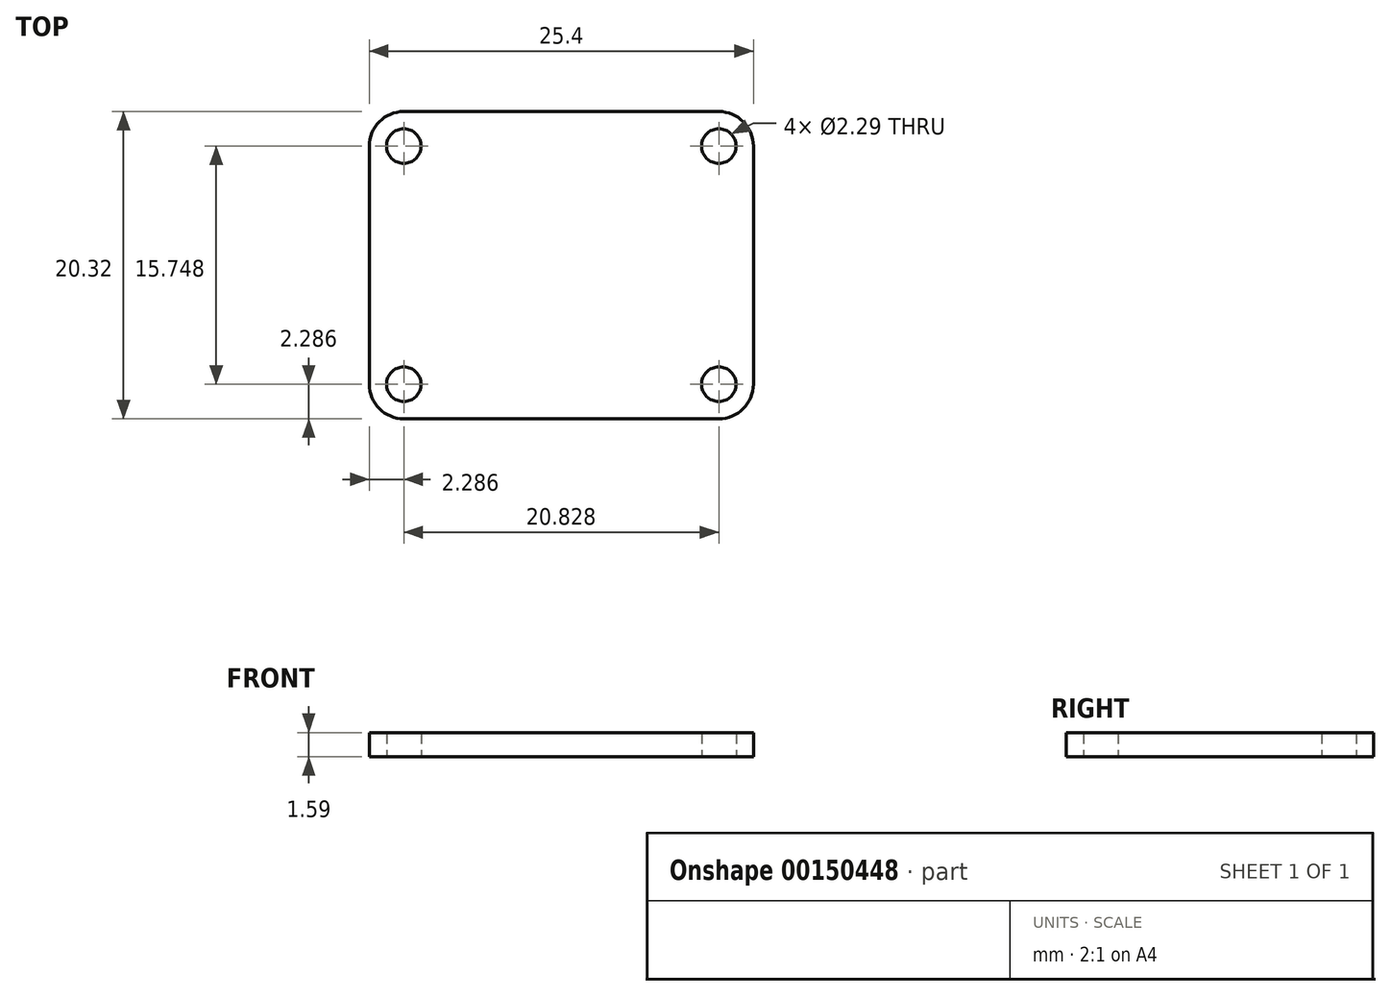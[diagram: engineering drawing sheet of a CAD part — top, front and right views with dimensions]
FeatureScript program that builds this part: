
annotation { "Feature Type Name" : "Feature", "Feature Type Description" : "" }
export const myFeature = defineFeature(function(context is Context, id is Id, definition is map)
    precondition{}
    {
        {
            var Q0;
            Q0=qCreatedBy(makeId("Top.planeOp"),FACE);
            var sketch = newSketch(context, id + "F0", { "sketchPlane" : qUnion([Q0])});
            skLineSegment(sketch, "E0.bottom", {"start": v(2.29, 0) * mm, "end": v(23.11, 0) * mm});
            skLineSegment(sketch, "E0.top", {"start": v(2.29, 20.32) * mm, "end": v(23.11, 20.32) * mm});
            skLineSegment(sketch, "E0.left", {"start": v(0, 2.29) * mm, "end": v(0, 18.03) * mm});
            skLineSegment(sketch, "E0.right", {"start": v(25.4, 2.29) * mm, "end": v(25.4, 18.03) * mm});
            skPoint(sketch, "E1.visualSharp", {"position": v(0, 20.32) * mm});
            skArc(sketch, "E1.filletArc", {"start": v(2.29, 20.32) * mm, "mid": v(0.67, 19.65) * mm, "end": v(0, 18.03) * mm});
            skPoint(sketch, "E2.visualSharp", {"position": v(25.4, 20.32) * mm});
            skArc(sketch, "E2.filletArc", {"start": v(25.4, 18.03) * mm, "mid": v(24.73, 19.65) * mm, "end": v(23.11, 20.32) * mm});
            skPoint(sketch, "E3.visualSharp", {"position": v(25.4, 0) * mm});
            skArc(sketch, "E3.filletArc", {"start": v(23.11, 0) * mm, "mid": v(24.73, 0.67) * mm, "end": v(25.4, 2.29) * mm});
            skPoint(sketch, "E4.visualSharp", {"position": v(0, 0) * mm});
            skArc(sketch, "E4.filletArc", {"start": v(0, 2.29) * mm, "mid": v(0.67, 0.67) * mm, "end": v(2.29, 0) * mm});
            skCircle(sketch, "E5", {"center": v(2.29, 18.03) * mm, "radius": 1.14 * mm});
            skCircle(sketch, "E6", {"center": v(23.11, 18.03) * mm, "radius": 1.14 * mm});
            skCircle(sketch, "E7", {"center": v(2.29, 2.29) * mm, "radius": 1.14 * mm});
            skCircle(sketch, "E8", {"center": v(23.11, 2.29) * mm, "radius": 1.14 * mm});
            skSolve(sketch);
        }
        {
            var Q0;
            Q0 = qSketchRegion(id + "F0", true);
            extrude(context, id + "F1", {"entities" : qUnion([Q0]), "depth" : 1.59 * mm});
        }
    });
